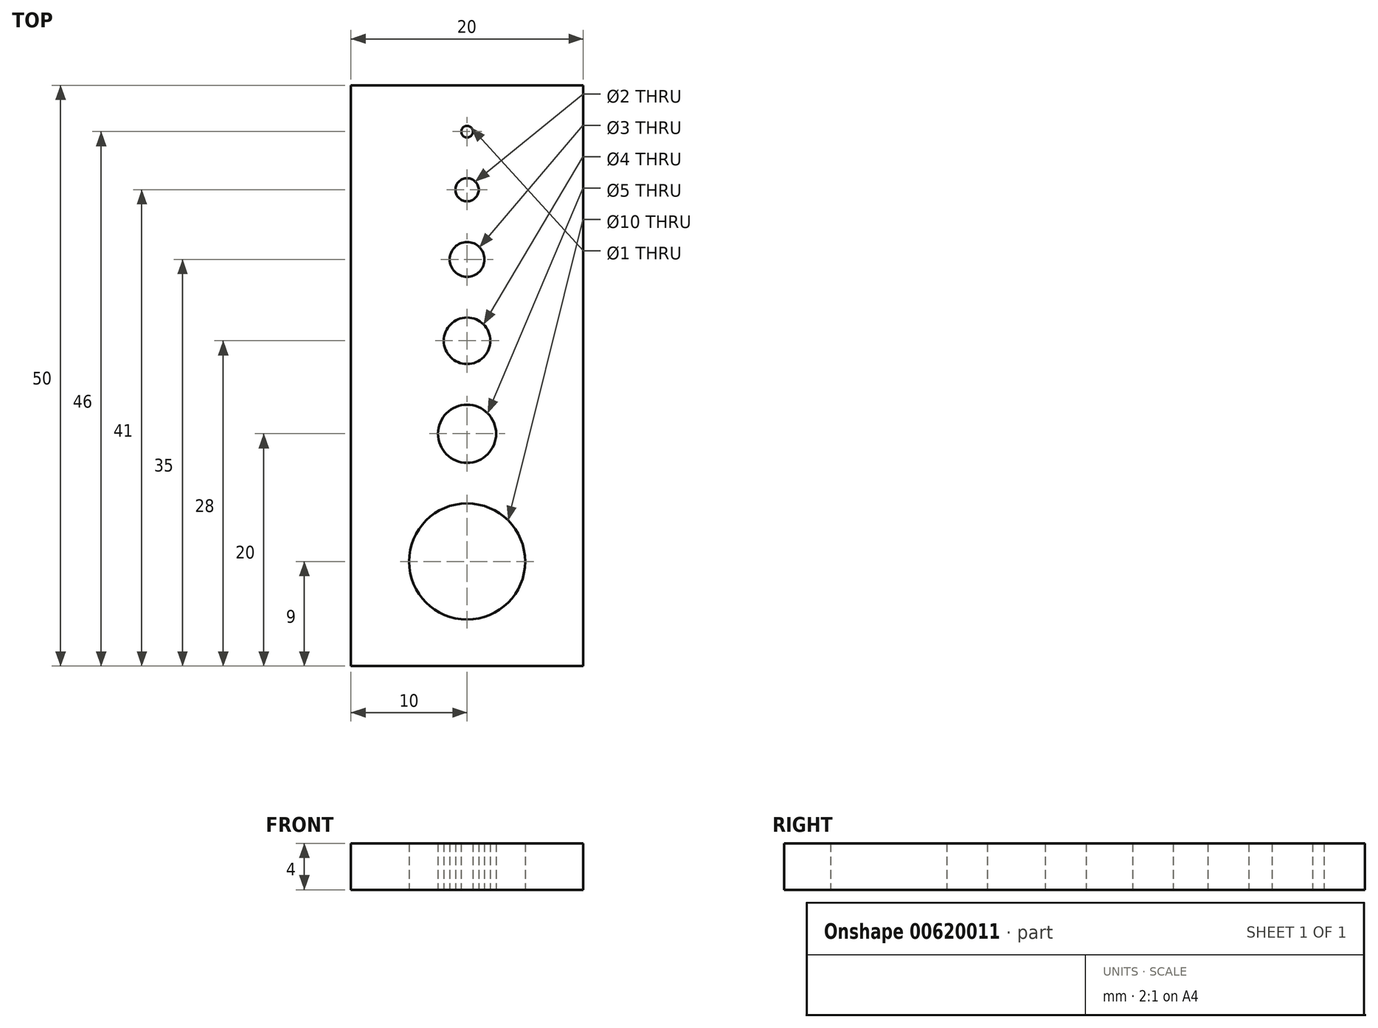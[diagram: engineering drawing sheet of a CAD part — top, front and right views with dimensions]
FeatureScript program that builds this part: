
annotation { "Feature Type Name" : "Feature", "Feature Type Description" : "" }
export const myFeature = defineFeature(function(context is Context, id is Id, definition is map)
    precondition{}
    {
        {
            var Q0;
            Q0=qCreatedBy(makeId("Top.planeOp"),FACE);
            var sketch = newSketch(context, id + "F0", { "sketchPlane" : qUnion([Q0])});
            skLineSegment(sketch, "E0", {"start": v(0, 0) * mm, "end": v(-20, 0) * mm});
            skLineSegment(sketch, "E1", {"start": v(-20, 0) * mm, "end": v(-20, 50) * mm});
            skLineSegment(sketch, "E2", {"start": v(-20, 50) * mm, "end": v(0, 50) * mm});
            skLineSegment(sketch, "E3", {"start": v(0, 50) * mm, "end": v(0, 0) * mm});
            skCircle(sketch, "E4", {"center": v(-10, 9) * mm, "radius": 5 * mm});
            skPoint(sketch, "E4.centerSnap0", {"position": v(-10, 0) * mm});
            skCircle(sketch, "E5", {"center": v(-10, 20) * mm, "radius": 2.5 * mm});
            skCircle(sketch, "E6", {"center": v(-10, 28) * mm, "radius": 2 * mm});
            skCircle(sketch, "E7", {"center": v(-10, 35) * mm, "radius": 1.5 * mm});
            skCircle(sketch, "E8", {"center": v(-10, 41) * mm, "radius": 1 * mm});
            skCircle(sketch, "E9", {"center": v(-10, 46) * mm, "radius": 0.5 * mm});
            skSolve(sketch);
        }
        {
            var Q0;
            Q0=makeQuery(id+"F0.imprint","IMPRINT",FACE,{"disambiguationData":[TD([[makeQuery(id+"F0.imprint","IMPRINT",EDGE,{"derivedFrom":sQuery(id+"F0.wireOp",EDGE,"E0")}),-1.0]])]});
            extrude(context, id + "F1", {"entities" : qUnion([Q0]), "depth" : 4 * mm, "offsetDistance" : 25 * mm});
        }
    });
